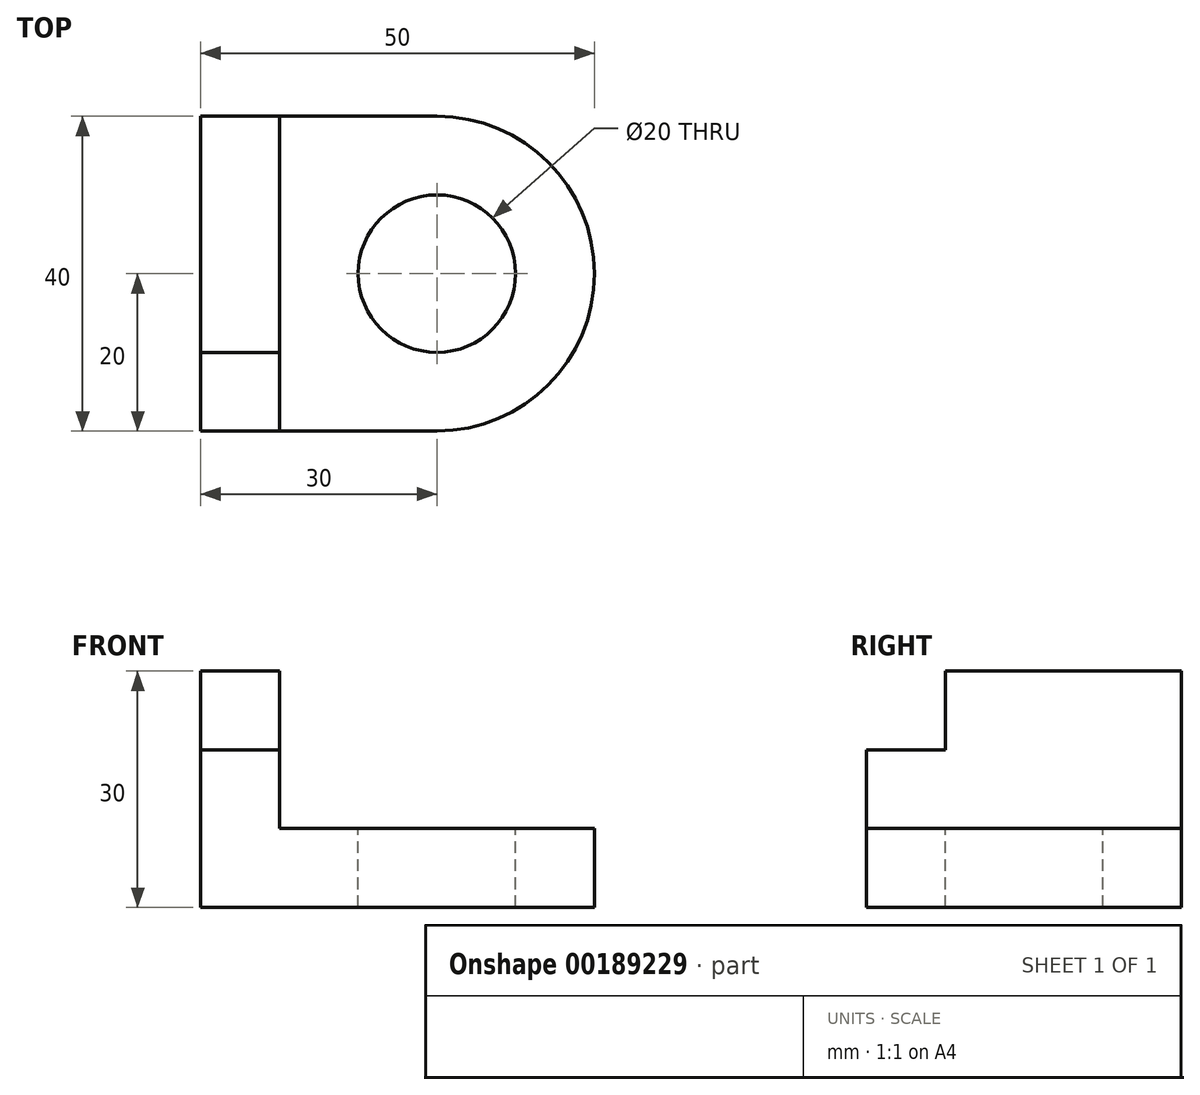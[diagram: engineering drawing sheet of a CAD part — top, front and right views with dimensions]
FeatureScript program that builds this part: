
annotation { "Feature Type Name" : "Feature", "Feature Type Description" : "" }
export const myFeature = defineFeature(function(context is Context, id is Id, definition is map)
    precondition{}
    {
        {
            var Q0;
            Q0=qCreatedBy(makeId("Front.planeOp"),FACE);
            var sketch = newSketch(context, id + "F0", { "sketchPlane" : qUnion([Q0])});
            skLineSegment(sketch, "E0", {"start": v(0, 0) * mm, "end": v(0, 30) * mm});
            skLineSegment(sketch, "E1", {"start": v(0, 30) * mm, "end": v(10, 30) * mm});
            skLineSegment(sketch, "E2", {"start": v(10, 30) * mm, "end": v(10, 10) * mm});
            skLineSegment(sketch, "E3", {"start": v(10, 10) * mm, "end": v(50, 10) * mm});
            skLineSegment(sketch, "E4", {"start": v(50, 10) * mm, "end": v(50, 0) * mm});
            skLineSegment(sketch, "E5", {"start": v(50, 0) * mm, "end": v(0, 0) * mm});
            skSolve(sketch);
        }
        {
            var Q0;
            Q0=makeQuery(id+"F0.imprint","IMPRINT",FACE,{"disambiguationData":[TD([[makeQuery(id+"F0.imprint","IMPRINT",EDGE,{"derivedFrom":sQuery(id+"F0.wireOp",EDGE,"E0")}),-1.0]])]});
            extrude(context, id + "F1", {"entities" : qUnion([Q0]), "endBound" : BoundingType.SYMMETRIC, "depth" : 40 * mm});
        }
        {
            var Q0;
            Q0=makeQuery(id+"F1.opExtrude","CAP_EDGE",EDGE,{"disambiguationData":[OSD([sQuery(id+"F0.wireOp",EDGE,"E4")])],"isStart":false});
            var Q1;
            Q1=makeQuery(id+"F1.opExtrude","CAP_EDGE",EDGE,{"disambiguationData":[OSD([sQuery(id+"F0.wireOp",EDGE,"E4")])],"isStart":true});
            fillet(context, id + "F2", {"entities" : qUnion([Q0, Q1]), "radius" : 20 * mm, "tangentPropagation" : true, "allowEdgeOverflow" : false});
        }
        {
            var Q0;
            Q0=makeQuery(id+"F1.opExtrude","SWEPT_FACE",FACE,{"disambiguationData":[OSD([sQuery(id+"F0.wireOp",EDGE,"E3")])]});
            var sketch = newSketch(context, id + "F3", { "sketchPlane" : qUnion([Q0])});
            skCircle(sketch, "E6", {"center": v(30, 0) * mm, "radius": 10 * mm});
            skSolve(sketch);
        }
        {
            var Q0;
            Q0=makeQuery(id+"F3.imprint","IMPRINT",FACE,{"disambiguationData":[TD([[makeQuery(id+"F3.imprint","IMPRINT",EDGE,{"derivedFrom":sQuery(id+"F3.wireOp",EDGE,"E6")}),1.0]])]});
            extrude(context, id + "F4", {"entities" : qUnion([Q0]), "operationType" : NewBodyOperationType.REMOVE, "endBound" : BoundingType.UP_TO_NEXT, "oppositeDirection" : true, "depth" : 25 * mm});
        }
        {
            var Q0;
            Q0=makeQuery(id+"F1.opExtrude","SWEPT_FACE",FACE,{"disambiguationData":[OSD([sQuery(id+"F0.wireOp",EDGE,"E2")])]});
            var sketch = newSketch(context, id + "F5", { "sketchPlane" : qUnion([Q0])});
            skLineSegment(sketch, "E7.bottom", {"start": v(-20, 30) * mm, "end": v(-10, 30) * mm});
            skLineSegment(sketch, "E7.top", {"start": v(-20, 20) * mm, "end": v(-10, 20) * mm});
            skLineSegment(sketch, "E7.left", {"start": v(-20, 30) * mm, "end": v(-20, 20) * mm});
            skLineSegment(sketch, "E7.right", {"start": v(-10, 30) * mm, "end": v(-10, 20) * mm});
            skSolve(sketch);
        }
        {
            var Q0;
            Q0=makeQuery(id+"F5.imprint","IMPRINT",FACE,{"disambiguationData":[TD([[makeQuery(id+"F5.imprint","IMPRINT",EDGE,{"derivedFrom":sQuery(id+"F5.wireOp",EDGE,"E7.bottom")}),-1.0]])]});
            extrude(context, id + "F6", {"entities" : qUnion([Q0]), "operationType" : NewBodyOperationType.REMOVE, "endBound" : BoundingType.UP_TO_NEXT, "oppositeDirection" : true, "depth" : 25 * mm});
        }
    });
